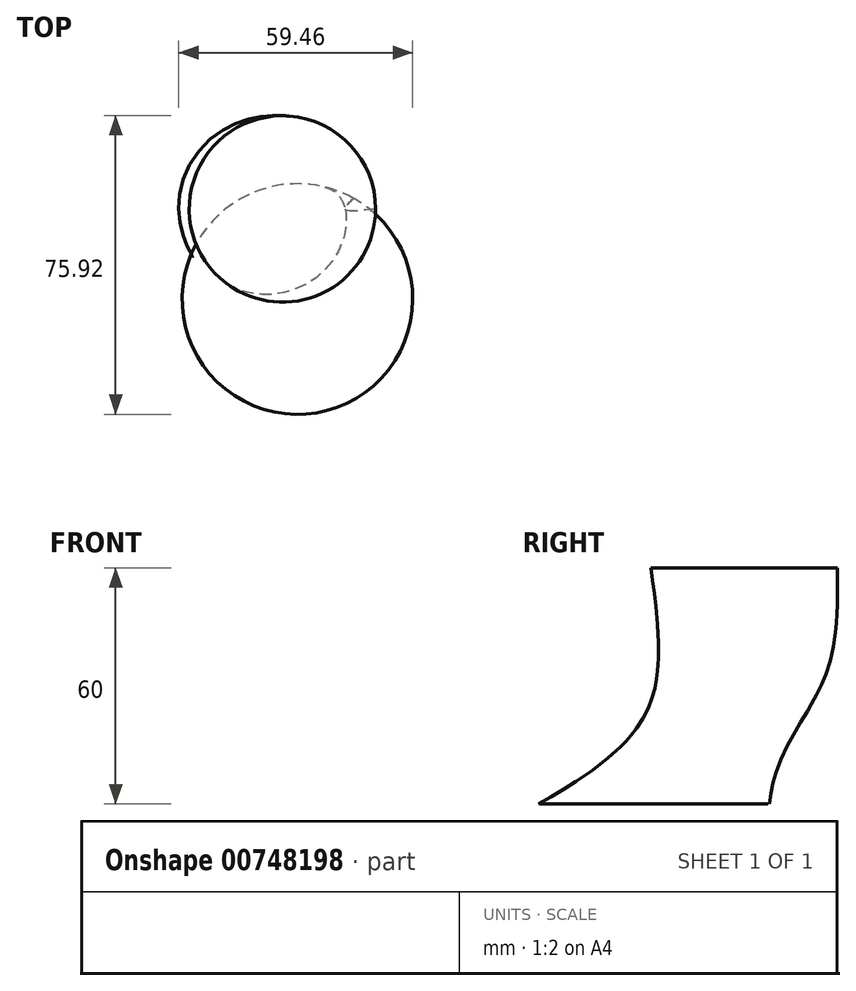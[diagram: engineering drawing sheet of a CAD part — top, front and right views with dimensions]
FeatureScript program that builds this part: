
annotation { "Feature Type Name" : "Feature", "Feature Type Description" : "" }
export const myFeature = defineFeature(function(context is Context, id is Id, definition is map)
    precondition{}
    {
        {
            var Q0;
            Q0=qCreatedBy(makeId("Top.planeOp"),FACE);
            cPlane(context, id + "F0", {"entities" : qUnion([Q0]), "cplaneType" : CPlaneType.OFFSET, "offset" : 30 * mm, "width" : 150 * mm, "height" : 150 * mm});
        }
        {
            var Q0;
            Q0=qCreatedBy(id+"F0.planeOp",FACE);
            cPlane(context, id + "F1", {"entities" : qUnion([Q0]), "cplaneType" : CPlaneType.OFFSET, "offset" : 30 * mm, "width" : 150 * mm, "height" : 150 * mm});
        }
        {
            var Q0;
            Q0=qCreatedBy(makeId("Top.planeOp"),FACE);
            var sketch = newSketch(context, id + "F2", { "sketchPlane" : qUnion([Q0])});
            skCircle(sketch, "E0", {"center": v(-9.1, 14.3) * mm, "radius": 29.29 * mm});
            skSolve(sketch);
        }
        {
            var Q0;
            Q0=qCreatedBy(id+"F0.planeOp",FACE);
            var sketch = newSketch(context, id + "F3", { "sketchPlane" : qUnion([Q0])});
            skCircle(sketch, "E1", {"center": v(-17.57, 35.67) * mm, "radius": 21.04 * mm});
            skSolve(sketch);
        }
        {
            var Q0;
            Q0=qCreatedBy(id+"F1.planeOp",FACE);
            var sketch = newSketch(context, id + "F4", { "sketchPlane" : qUnion([Q0])});
            skCircle(sketch, "E2", {"center": v(-12.9, 37.19) * mm, "radius": 23.67 * mm});
            skSolve(sketch);
        }
        {
            var Q0;
            Q0=makeQuery(id+"F4.imprint","IMPRINT",FACE,{"disambiguationData":[TD([[makeQuery(id+"F4.imprint","IMPRINT",EDGE,{"derivedFrom":sQuery(id+"F4.wireOp",EDGE,"E2")}),1.0]])]});
            var Q1;
            Q1=makeQuery(id+"F3.imprint","IMPRINT",FACE,{"disambiguationData":[TD([[makeQuery(id+"F3.imprint","IMPRINT",EDGE,{"derivedFrom":sQuery(id+"F3.wireOp",EDGE,"E1")}),1.0]])]});
            var Q2;
            Q2=makeQuery(id+"F2.imprint","IMPRINT",FACE,{"disambiguationData":[TD([[makeQuery(id+"F2.imprint","IMPRINT",EDGE,{"derivedFrom":sQuery(id+"F2.wireOp",EDGE,"E0")}),1.0]])]});
            loft(context, id + "F5", {"sheetProfilesArray" : [{ "sheetProfileEntities" : qUnion([Q0]) }, { "sheetProfileEntities" : qUnion([Q1]) }, { "sheetProfileEntities" : qUnion([Q2]) }]});
        }
    });
